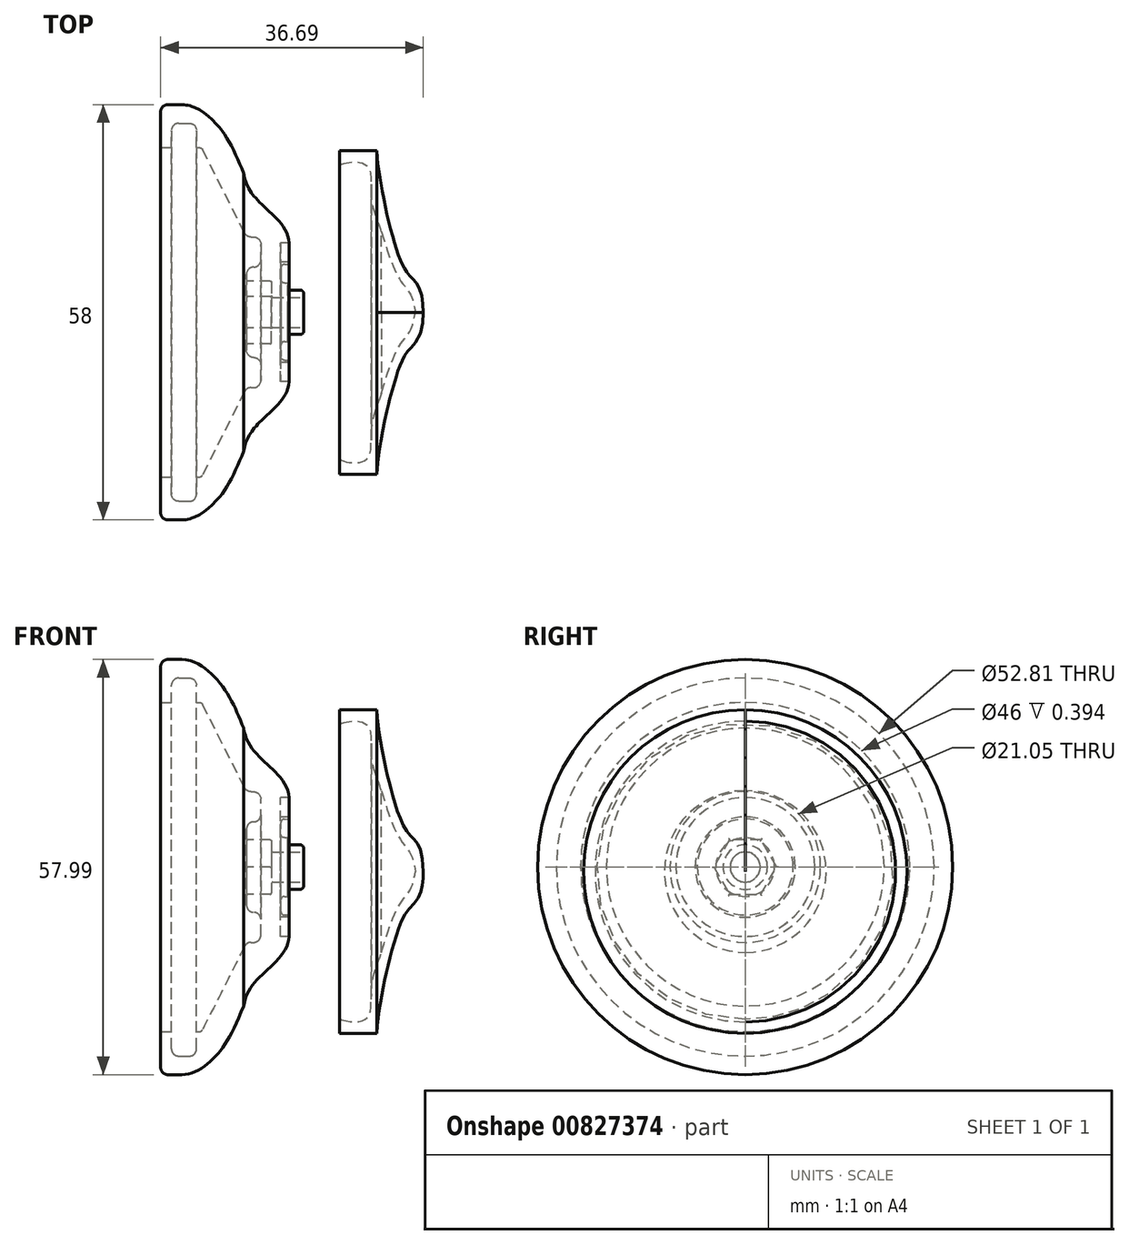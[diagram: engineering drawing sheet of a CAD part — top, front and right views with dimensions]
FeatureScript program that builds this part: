
annotation { "Feature Type Name" : "Feature", "Feature Type Description" : "" }
export const myFeature = defineFeature(function(context is Context, id is Id, definition is map)
    precondition{}
    {
        {
            var Q0;
            Q0=qCreatedBy(makeId("Front.planeOp"),FACE);
            var sketch = newSketch(context, id + "F0", { "sketchPlane" : qUnion([Q0])});
            skPoint(sketch, "E0", {"position": v(36.58, 0) * mm});
            skLineSegment(sketch, "E1", {"start": v(40.53, -3.31) * mm, "end": v(40.53, -2.81) * mm});
            skLineSegment(sketch, "E2", {"start": v(40.03, -2.31) * mm, "end": v(38.28, -2.31) * mm});
            skLineSegment(sketch, "E3", {"start": v(38.28, -2.31) * mm, "end": v(38.28, -1.31) * mm});
            skLineSegment(sketch, "E4", {"start": v(38.28, -1.31) * mm, "end": v(37.83, -1.31) * mm});
            skLineSegment(sketch, "E5", {"start": v(37.33, -0.81) * mm, "end": v(37.33, 0.78) * mm});
            skLineSegment(sketch, "E6", {"start": v(37.82, 1.28) * mm, "end": v(38.46, 1.29) * mm});
            skLineSegment(sketch, "E7", {"start": v(38.46, 1.29) * mm, "end": v(38.46, 1.59) * mm});
            skLineSegment(sketch, "E8", {"start": v(38.46, 1.59) * mm, "end": v(37.26, 1.59) * mm});
            skLineSegment(sketch, "E9", {"start": v(37.26, 1.59) * mm, "end": v(37.26, 4.29) * mm});
            skLineSegment(sketch, "E10", {"start": v(37.26, 4.29) * mm, "end": v(38.46, 4.29) * mm});
            skPoint(sketch, "E11.startSnap0", {"position": v(39.4, -2.31) * mm});
            skLineSegment(sketch, "E12", {"start": v(36.03, -3.31) * mm, "end": v(40.53, -3.31) * mm});
            skLineSegment(sketch, "E13", {"start": v(40.53, -5.41) * mm, "end": v(38.22, -5.41) * mm});
            skLineSegment(sketch, "E14", {"start": v(40.53, -5.41) * mm, "end": v(20.53, -5.41) * mm});
            skLineSegment(sketch, "E15", {"start": v(21.52, 23.58) * mm, "end": v(23.5, 23.58) * mm});
            skFitSpline(sketch, "E16", {"points": [v(23.5, 23.58) * mm, v(27.76, 21.46) * mm, v(32.12, 14) * mm], "startDerivative": vector(10.57, 0) * mm, "endDerivative": vector(7.95, -20.2) * mm});
            skFitSpline(sketch, "E17", {"points": [v(32.12, 14) * mm, v(35.32, 9.04) * mm, v(38.46, 4.29) * mm], "startDerivative": vector(2.45, -14.07) * mm, "endDerivative": vector(0, -11.09) * mm});
            skLineSegment(sketch, "E18", {"start": v(32.53, -0.77) * mm, "end": v(32.53, -3.31) * mm});
            skLineSegment(sketch, "E19", {"start": v(20.53, 22.58) * mm, "end": v(20.54, 17.58) * mm});
            skLineSegment(sketch, "E20", {"start": v(20.54, 17.58) * mm, "end": v(22.04, 17.59) * mm});
            skLineSegment(sketch, "E21", {"start": v(22.04, 17.59) * mm, "end": v(22.04, 19.99) * mm});
            skLineSegment(sketch, "E22", {"start": v(23.04, 20.99) * mm, "end": v(24.54, 20.99) * mm});
            skLineSegment(sketch, "E23", {"start": v(25.54, 19.99) * mm, "end": v(25.54, 17.58) * mm});
            skPoint(sketch, "E24.visualSharp", {"position": v(22.04, 20.99) * mm});
            skArc(sketch, "E24.filletArc", {"start": v(23.04, 20.99) * mm, "mid": v(22.34, 20.7) * mm, "end": v(22.04, 19.99) * mm});
            skPoint(sketch, "E25.visualSharp", {"position": v(25.54, 20.99) * mm});
            skArc(sketch, "E25.filletArc", {"start": v(25.54, 19.99) * mm, "mid": v(25.25, 20.7) * mm, "end": v(24.54, 20.99) * mm});
            skArc(sketch, "E26.filletArc", {"start": v(21.52, 23.58) * mm, "mid": v(20.82, 23.3) * mm, "end": v(20.53, 22.58) * mm});
            skLineSegment(sketch, "E27", {"start": v(25.54, 17.58) * mm, "end": v(25.94, 17.58) * mm});
            skLineSegment(sketch, "E28", {"start": v(26.38, 17.31) * mm, "end": v(32.25, 5.66) * mm});
            skLineSegment(sketch, "E29", {"start": v(33.14, 5.1) * mm, "end": v(33.53, 5.1) * mm});
            skLineSegment(sketch, "E30", {"start": v(34.53, 4.1) * mm, "end": v(34.53, 1.9) * mm});
            skLineSegment(sketch, "E31", {"start": v(33.53, 0.9) * mm, "end": v(33.53, 0.9) * mm});
            skLineSegment(sketch, "E32", {"start": v(32.53, -0.1) * mm, "end": v(32.53, -0.57) * mm});
            skPoint(sketch, "E33.visualSharp", {"position": v(32.53, 5.1) * mm});
            skArc(sketch, "E33.filletArc", {"start": v(32.25, 5.66) * mm, "mid": v(32.62, 5.26) * mm, "end": v(33.14, 5.1) * mm});
            skPoint(sketch, "E34.visualSharp", {"position": v(34.53, 5.1) * mm});
            skArc(sketch, "E34.filletArc", {"start": v(34.53, 4.1) * mm, "mid": v(34.24, 4.82) * mm, "end": v(33.53, 5.1) * mm});
            skPoint(sketch, "E35.visualSharp", {"position": v(34.53, 0.9) * mm});
            skArc(sketch, "E35.filletArc", {"start": v(33.53, 0.9) * mm, "mid": v(34.24, 1.2) * mm, "end": v(34.53, 1.9) * mm});
            skPoint(sketch, "E36.visualSharp", {"position": v(32.53, 0.9) * mm});
            skArc(sketch, "E36.filletArc", {"start": v(33.53, 0.9) * mm, "mid": v(32.82, 0.61) * mm, "end": v(32.53, -0.1) * mm});
            skPoint(sketch, "E37.visualSharp", {"position": v(32.53, -0.77) * mm});
            skPoint(sketch, "E38.visualSharp", {"position": v(35.53, -3.31) * mm});
            skPoint(sketch, "E39.visualSharp", {"position": v(37.33, -1.31) * mm});
            skArc(sketch, "E39.filletArc", {"start": v(37.33, -0.81) * mm, "mid": v(37.48, -1.17) * mm, "end": v(37.83, -1.31) * mm});
            skArc(sketch, "E40.filletArc", {"start": v(37.82, 1.28) * mm, "mid": v(37.47, 1.13) * mm, "end": v(37.33, 0.78) * mm});
            skPoint(sketch, "E41.visualSharp", {"position": v(40.53, -2.31) * mm});
            skArc(sketch, "E41.filletArc", {"start": v(40.53, -2.81) * mm, "mid": v(40.38, -2.46) * mm, "end": v(40.03, -2.31) * mm});
            skPoint(sketch, "E42.visualSharp", {"position": v(26.24, 17.58) * mm});
            skArc(sketch, "E42.filletArc", {"start": v(26.38, 17.31) * mm, "mid": v(26.2, 17.51) * mm, "end": v(25.94, 17.58) * mm});
            skLineSegment(sketch, "E43", {"start": v(36.03, -3.31) * mm, "end": v(32.53, -3.31) * mm});
            skLineSegment(sketch, "E44", {"start": v(32.53, -0.57) * mm, "end": v(32.53, -0.77) * mm});
            skPoint(sketch, "E45.orphan", {"position": v(32.53, -5.41) * mm});
            skSolve(sketch);
        }
        {
            var Q0;
            Q0=qCreatedBy(makeId("Front.planeOp"),FACE);
            var sketch = newSketch(context, id + "F1", { "sketchPlane" : qUnion([Q0])});
            skLineSegment(sketch, "E46", {"start": v(45.52, -6.03) * mm, "end": v(45.52, 16.57) * mm});
            skLineSegment(sketch, "E47", {"start": v(45.52, 16.57) * mm, "end": v(57.22, 16.57) * mm});
            skLineSegment(sketch, "E48", {"start": v(57.22, 16.57) * mm, "end": v(57.22, -6.03) * mm});
            skLineSegment(sketch, "E49", {"start": v(57.22, -6.03) * mm, "end": v(45.52, -6.03) * mm});
            skLineSegment(sketch, "E50", {"start": v(45.52, 16.57) * mm, "end": v(50.72, 16.57) * mm});
            skLineSegment(sketch, "E51", {"start": v(45.52, 16.57) * mm, "end": v(45.52, 14.57) * mm});
            skPoint(sketch, "E52.1.internal.snap0", {"position": v(48.12, 16.57) * mm});
            skFitSpline(sketch, "E53", {"points": [v(45.52, 14.57) * mm, v(49.42, 14.37) * mm, v(49.98, 10.23) * mm, v(51.39, 5.27) * mm], "startDerivative": vector(14.16, 5.38) * mm, "endDerivative": vector(5.05, -15.1) * mm});
            skFitSpline(sketch, "E54", {"points": [v(51.39, 5.27) * mm, v(53.79, -1.19) * mm, v(55.5, -3.64) * mm, v(56.14, -6.03) * mm], "startDerivative": vector(3.62, -12.47) * mm, "endDerivative": vector(1.6, -7.9) * mm});
            skFitSpline(sketch, "E55", {"points": [v(50.72, 16.57) * mm, v(51.63, 10.15) * mm, v(52.8, 5.16) * mm, v(55.04, -0.56) * mm, v(57.22, -6.03) * mm], "startDerivative": vector(1.32, -24.15) * mm, "endDerivative": vector(0, -48.08) * mm});
            skSolve(sketch);
        }
        {
            var Q0;
            {var subQ0=sQuery(id+"F1.wireOp",EDGE,"E53");Q0=makeQuery(id+"F1.imprint","IMPRINT",FACE,{"disambiguationData":[TD([[makeQuery(id+"F1.imprint","IMPRINT",EDGE,{"derivedFrom":subQ0}),1.0]])]});}
            var Q1;
            Q1=sQuery(id+"F1.wireOp",EDGE,"E49");
            revolve(context, id + "F2", {"surfaceOperationType" : NewSurfaceOperationType.NEW, "entities" : qUnion([Q0]), "axis" : qUnion([Q1]), "revolveType" : RevolveType.FULL});
        }
        {
            var Q0;
            Q0=qSketchRegion(id+"F0",true);
            var Q1;
            Q1=sQuery(id+"F0.wireOp",EDGE,"E14");
            revolve(context, id + "F3", {"surfaceOperationType" : NewSurfaceOperationType.NEW, "entities" : qUnion([Q0]), "axis" : qUnion([Q1]), "revolveType" : RevolveType.FULL});
        }
        {
            var Q0;
            Q0=makeQuery(id+"F3.opRevolve","SWEPT_FACE",FACE,{"disambiguationData":[OSD([sQuery(id+"F0.wireOp",EDGE,"E18"),sQuery(id+"F0.wireOp",EDGE,"E32"),sQuery(id+"F0.wireOp",EDGE,"E44")])]});
            var sketch = newSketch(context, id + "F4", { "sketchPlane" : qUnion([Q0])});
            skPoint(sketch, "E56.0.midPoint", {"position": v(0, -1.31) * mm});
            skLineSegment(sketch, "E57.0", {"start": v(2.2, -9.21) * mm, "end": v(-2.2, -9.21) * mm});
            skLineSegment(sketch, "E57.1", {"start": v(-2.2, -9.21) * mm, "end": v(-4.39, -5.41) * mm});
            skLineSegment(sketch, "E57.2", {"start": v(-4.39, -5.41) * mm, "end": v(-2.2, -1.61) * mm});
            skLineSegment(sketch, "E57.3", {"start": v(-2.2, -1.61) * mm, "end": v(2.2, -1.61) * mm});
            skLineSegment(sketch, "E57.4", {"start": v(2.2, -1.61) * mm, "end": v(4.39, -5.41) * mm});
            skLineSegment(sketch, "E57.5", {"start": v(4.39, -5.41) * mm, "end": v(2.2, -9.21) * mm});
            skPoint(sketch, "E57.0.midPoint", {"position": v(0, -9.21) * mm});
            skSolve(sketch);
        }
        {
            var Q0;
            Q0=makeQuery(id+"F4.imprint","IMPRINT",FACE,{"disambiguationData":[TD([[makeQuery(id+"F4.imprint","IMPRINT",EDGE,{"derivedFrom":sQuery(id+"F4.wireOp",EDGE,"E57.0")}),-1.0]])]});
            extrude(context, id + "F5", {"entities" : qUnion([Q0]), "operationType" : NewBodyOperationType.REMOVE, "oppositeDirection" : true, "depth" : 3.5 * mm, "offsetDistance" : 25 * mm});
        }
        {
            var Q0;
            Q0=makeQuery(id+"F5.boolean.opBoolean","COPY",FACE,{"derivedFrom":makeQuery(id+"F5.opExtrude","CAP_FACE",FACE,{"disambiguationData":[OSD([sQuery(id+"F0.wireOp",EDGE,"E18"),sQuery(id+"F0.wireOp",EDGE,"E43"),sQuery(id+"F4.wireOp",EDGE,"E56.0"),sQuery(id+"F4.wireOp",EDGE,"E56.1"),sQuery(id+"F4.wireOp",EDGE,"E56.2"),sQuery(id+"F4.wireOp",EDGE,"E56.3"),sQuery(id+"F4.wireOp",EDGE,"E56.4"),sQuery(id+"F4.wireOp",EDGE,"E56.5")])],"isStart":false})});
            fillet(context, id + "F6", {"entities" : qUnion([Q0]), "radius" : .2 * mm, "tangentPropagation" : true, "allowEdgeOverflow" : false});
        }
        {
            var Q0;
            Q0=makeQuery(id+"F3.opRevolve","SWEPT_FACE",FACE,{"disambiguationData":[OSD([sQuery(id+"F0.wireOp",EDGE,"E18"),sQuery(id+"F0.wireOp",EDGE,"E32"),sQuery(id+"F0.wireOp",EDGE,"E44")])]});
            fillet(context, id + "F7", {"entities" : qUnion([Q0]), "radius" : .2 * mm, "tangentPropagation" : true, "allowEdgeOverflow" : false});
        }
        {
            var Q0;
            Q0=makeQuery(id+"F2.opRevolve","SWEPT_EDGE",EDGE,{"disambiguationData":[OSD([sQuery(id+"F1.wireOp",EDGE,"E46"),sQuery(id+"F1.wireOp",EDGE,"E53")])]});
            fillet(context, id + "F8", {"entities" : qUnion([Q0]), "radius" : .2 * mm, "tangentPropagation" : true, "allowEdgeOverflow" : false});
        }
    });
